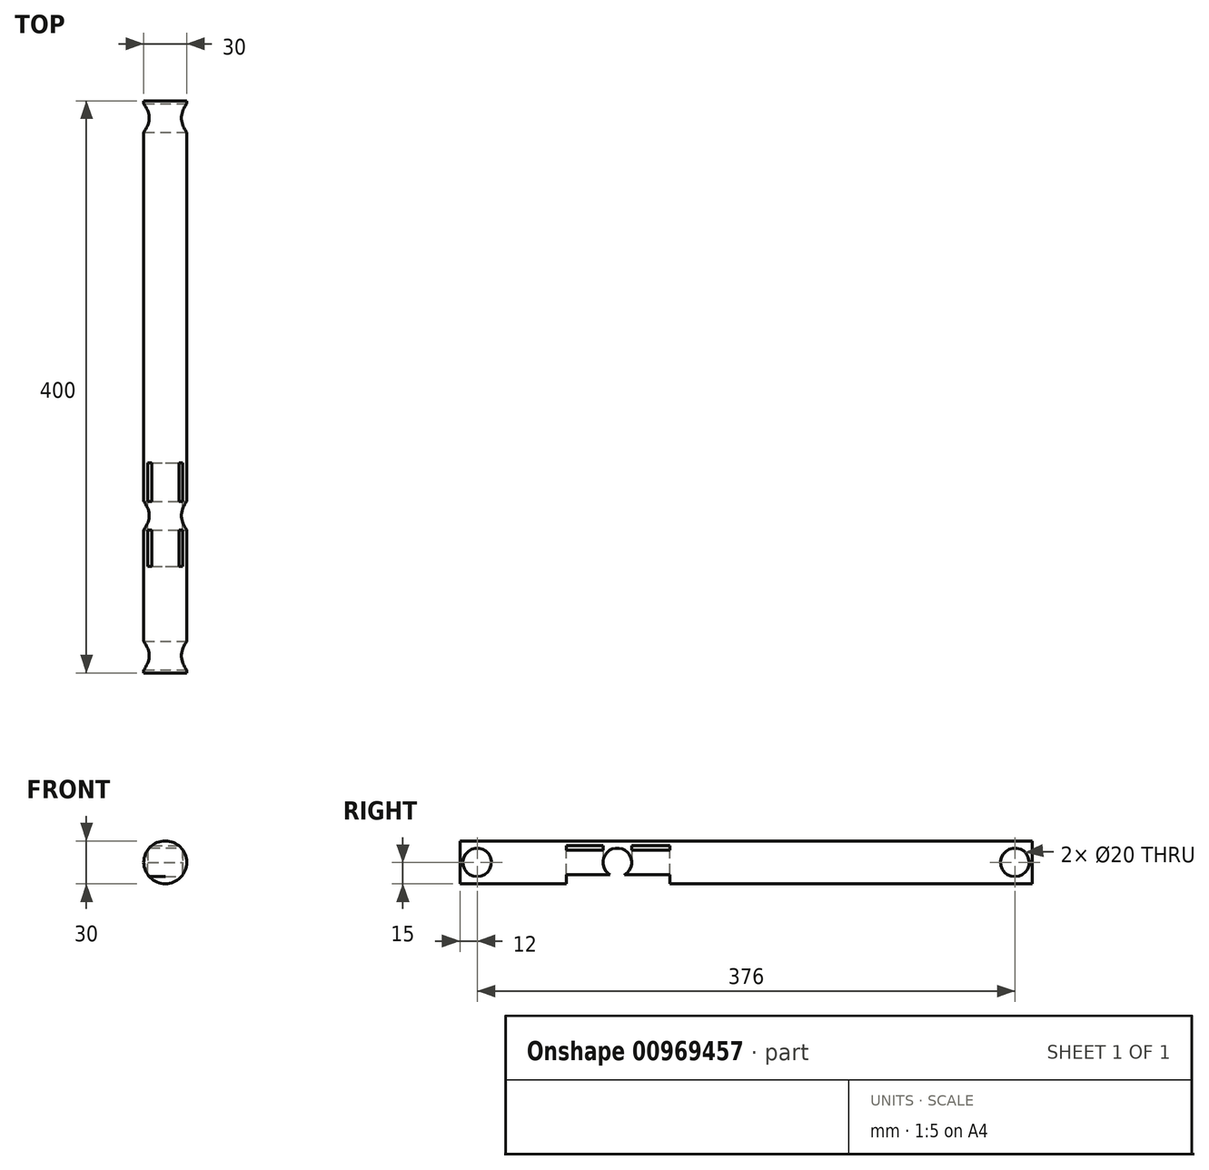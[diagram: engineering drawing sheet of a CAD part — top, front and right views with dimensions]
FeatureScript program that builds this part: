
annotation { "Feature Type Name" : "Feature", "Feature Type Description" : "" }
export const myFeature = defineFeature(function(context is Context, id is Id, definition is map)
    precondition{}
    {
        {
            var Q0;
            Q0=qCreatedBy(makeId("Front.planeOp"),FACE);
            var sketch = newSketch(context, id + "F0", { "sketchPlane" : qUnion([Q0])});
            skCircle(sketch, "E0", {"center": v(0, 0) * mm, "radius": 15 * mm});
            skSolve(sketch);
        }
        {
            var Q0;
            Q0 = qSketchRegion(id + "F0", true);
            extrude(context, id + "F1", {"entities" : qUnion([Q0]), "endBound" : BoundingType.SYMMETRIC, "depth" : 400 * mm, "offsetDistance" : 25 * mm});
        }
        {
            var Q0;
            Q0=qCreatedBy(makeId("Right.planeOp"),FACE);
            var sketch = newSketch(context, id + "F2", { "sketchPlane" : qUnion([Q0])});
            skCircle(sketch, "E1", {"center": v(188, 0) * mm, "radius": 10 * mm});
            skLineSegment(sketch, "E2", {"start": v(0, 8.8) * mm, "end": v(0, -8.32) * mm, "construction": true});
            skCircle(sketch, "E3.MirrorC", {"center": v(-188, 0) * mm, "radius": 10 * mm});
            skSolve(sketch);
        }
        {
            var Q0;
            Q0 = qSketchRegion(id + "F2", true);
            extrude(context, id + "F3", {"entities" : qUnion([Q0]), "operationType" : NewBodyOperationType.REMOVE, "endBound" : BoundingType.SYMMETRIC, "oppositeDirection" : true, "depth" : 400 * mm, "offsetDistance" : 25 * mm});
        }
        {
            var Q0;
            Q0=qCreatedBy(makeId("Right.planeOp"),FACE);
            var sketch = newSketch(context, id + "F4", { "sketchPlane" : qUnion([Q0])});
            skCircle(sketch, "E4", {"center": v(-90, 0) * mm, "radius": 10 * mm});
            skSolve(sketch);
        }
        {
            var Q0;
            Q0 = qSketchRegion(id + "F4", true);
            extrude(context, id + "F5", {"entities" : qUnion([Q0]), "operationType" : NewBodyOperationType.REMOVE, "endBound" : BoundingType.SYMMETRIC, "oppositeDirection" : true, "depth" : 400 * mm, "offsetDistance" : 25 * mm});
        }
        {
            var Q0;
            Q0=qCreatedBy(makeId("Top.planeOp"),FACE);
            var sketch = newSketch(context, id + "F6", { "sketchPlane" : qUnion([Q0])});
            skLineSegment(sketch, "E5.bottom", {"start": v(-12.29, -125.56) * mm, "end": v(12.29, -125.56) * mm});
            skLineSegment(sketch, "E5.top", {"start": v(-12.29, -53.17) * mm, "end": v(12.29, -53.17) * mm});
            skLineSegment(sketch, "E5.left", {"start": v(-12.29, -125.56) * mm, "end": v(-12.29, -53.17) * mm});
            skLineSegment(sketch, "E5.right", {"start": v(12.29, -125.56) * mm, "end": v(12.29, -53.17) * mm});
            skPoint(sketch, "E5.middle", {"position": v(0, -89.37) * mm});
            skSolve(sketch);
        }
        {
            var Q0;
            Q0 = qSketchRegion(id + "F6", true);
            extrude(context, id + "F7", {"entities" : qUnion([Q0]), "operationType" : NewBodyOperationType.REMOVE, "oppositeDirection" : true, "depth" : 58.4 * mm, "offsetDistance" : 25 * mm});
        }
        {
            var Q0;
            {var subQ0=sQuery(id+"F6.wireOp",EDGE,"E5.top");var subQ1=sQuery(id+"F6.wireOp",EDGE,"E5.left");var subQ2=sQuery(id+"F6.wireOp",EDGE,"E5.right");Q0=makeQuery(id+"F7.boolean.opBoolean","COPY",FACE,{"disambiguationData":[TD([makeQuery(id+"F7.opExtrude","SWEPT_FACE",FACE,{"disambiguationData":[OSD([subQ0])]})])],"derivedFrom":makeQuery(id+"F7.opExtrude","CAP_FACE",FACE,{"disambiguationData":[OSD([sQuery(id+"F6.wireOp",EDGE,"E5.bottom"),subQ0,subQ1,subQ2])],"isStart":true})});}
            var Q1;
            {var subQ0=sQuery(id+"F6.wireOp",EDGE,"E5.bottom");var subQ1=sQuery(id+"F6.wireOp",EDGE,"E5.right");var subQ2=sQuery(id+"F6.wireOp",EDGE,"E5.left");Q1=makeQuery(id+"F7.boolean.opBoolean","COPY",FACE,{"disambiguationData":[TD([makeQuery(id+"F7.opExtrude","SWEPT_FACE",FACE,{"disambiguationData":[OSD([subQ0])]})])],"derivedFrom":makeQuery(id+"F7.opExtrude","CAP_FACE",FACE,{"disambiguationData":[OSD([subQ0,sQuery(id+"F6.wireOp",EDGE,"E5.top"),subQ2,subQ1])],"isStart":true})});}
            extrude(context, id + "F8", {"entities" : qUnion([Q0, Q1]), "operationType" : NewBodyOperationType.REMOVE, "oppositeDirection" : true, "depth" : 11.6 * mm, "offsetDistance" : 25 * mm});
        }
    });
